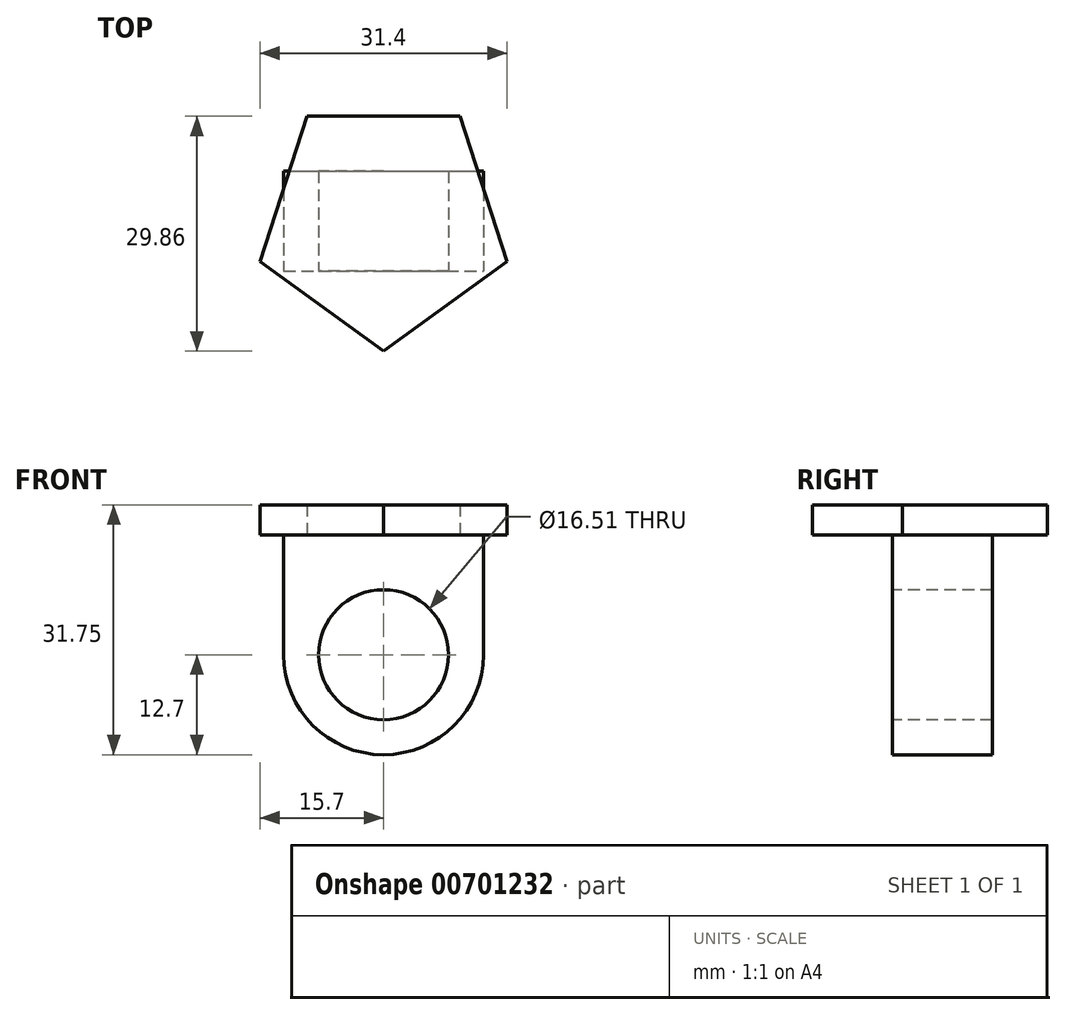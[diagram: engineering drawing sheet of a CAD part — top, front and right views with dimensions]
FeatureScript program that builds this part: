
annotation { "Feature Type Name" : "Feature", "Feature Type Description" : "" }
export const myFeature = defineFeature(function(context is Context, id is Id, definition is map)
    precondition{}
    {
        {
            var Q0;
            Q0=qCreatedBy(makeId("Top.planeOp"),FACE);
            var sketch = newSketch(context, id + "F0", { "sketchPlane" : qUnion([Q0])});
            skLineSegment(sketch, "E0.bottom", {"start": v(-12.7, 6.35) * mm, "end": v(12.7, 6.35) * mm});
            skLineSegment(sketch, "E0.top", {"start": v(-12.7, -6.35) * mm, "end": v(12.7, -6.35) * mm});
            skLineSegment(sketch, "E0.left", {"start": v(-12.7, 6.35) * mm, "end": v(-12.7, -6.35) * mm});
            skLineSegment(sketch, "E0.right", {"start": v(12.7, 6.35) * mm, "end": v(12.7, -6.35) * mm});
            skSolve(sketch);
        }
        {
            var Q0;
            Q0 = qSketchRegion(id + "F0", true);
            extrude(context, id + "F1", {"entities" : qUnion([Q0]), "depth" : 15.24 * mm, "offsetDistance" : 25.4 * mm});
        }
        {
            var Q0;
            Q0=makeQuery(id+"F1.opExtrude","SWEPT_FACE",FACE,{"disambiguationData":[OSD([sQuery(id+"F0.wireOp",EDGE,"E0.top")])]});
            var sketch = newSketch(context, id + "F2", { "sketchPlane" : qUnion([Q0])});
            skCircle(sketch, "E1", {"center": v(0, 0) * mm, "radius": 12.7 * mm});
            skSolve(sketch);
        }
        {
            var Q0;
            Q0 = qSketchRegion(id + "F2", true);
            extrude(context, id + "F3", {"entities" : qUnion([Q0]), "operationType" : NewBodyOperationType.ADD, "oppositeDirection" : true, "depth" : 12.7 * mm, "offsetDistance" : 25.4 * mm});
        }
        {
            var Q0;
            Q0=makeQuery(id+"F3.boolean.opBoolean","MERGE",FACE,{"derivedFrom":[makeQuery(id+"F1.opExtrude","SWEPT_FACE",FACE,{"disambiguationData":[OSD([sQuery(id+"F0.wireOp",EDGE,"E0.top")])]}),makeQuery(id+"F3.opExtrude","CAP_FACE",FACE,{"disambiguationData":[OSD([sQuery(id+"F2.wireOp",EDGE,"E1")])],"isStart":true})]});
            var sketch = newSketch(context, id + "F4", { "sketchPlane" : qUnion([Q0])});
            skCircle(sketch, "E2", {"center": v(0, 0) * mm, "radius": 8.26 * mm});
            skSolve(sketch);
        }
        {
            var Q0;
            Q0 = qSketchRegion(id + "F4", true);
            extrude(context, id + "F5", {"entities" : qUnion([Q0]), "operationType" : NewBodyOperationType.REMOVE, "oppositeDirection" : true, "depth" : 25.4 * mm, "offsetDistance" : 25.4 * mm});
        }
        {
            var Q0;
            Q0=makeQuery(id+"F1.opExtrude","CAP_FACE",FACE,{"disambiguationData":[OSD([sQuery(id+"F0.wireOp",EDGE,"E0.bottom"),sQuery(id+"F0.wireOp",EDGE,"E0.top"),sQuery(id+"F0.wireOp",EDGE,"E0.left"),sQuery(id+"F0.wireOp",EDGE,"E0.right")])],"isStart":false});
            var sketch = newSketch(context, id + "F6", { "sketchPlane" : qUnion([Q0])});
            skCircle(sketch, "E3.cCircle", {"center": v(0, 0) * mm, "radius": 13.35 * mm, "construction": true});
            skLineSegment(sketch, "E3.0", {"start": v(9.7, 13.35) * mm, "end": v(15.7, -5.1) * mm});
            skLineSegment(sketch, "E3.1", {"start": v(15.7, -5.1) * mm, "end": v(0, -16.5) * mm});
            skLineSegment(sketch, "E3.2", {"start": v(0, -16.5) * mm, "end": v(-15.7, -5.1) * mm});
            skLineSegment(sketch, "E3.3", {"start": v(-15.7, -5.1) * mm, "end": v(-9.7, 13.35) * mm});
            skLineSegment(sketch, "E3.4", {"start": v(-9.7, 13.35) * mm, "end": v(9.7, 13.35) * mm});
            skPoint(sketch, "E3.0.midPoint", {"position": v(12.7, 4.13) * mm});
            skSolve(sketch);
        }
        {
            var Q0;
            Q0 = qSketchRegion(id + "F6", true);
            extrude(context, id + "F7", {"entities" : qUnion([Q0]), "operationType" : NewBodyOperationType.ADD, "depth" : 3.8 * mm, "offsetDistance" : 25.4 * mm});
        }
    });
